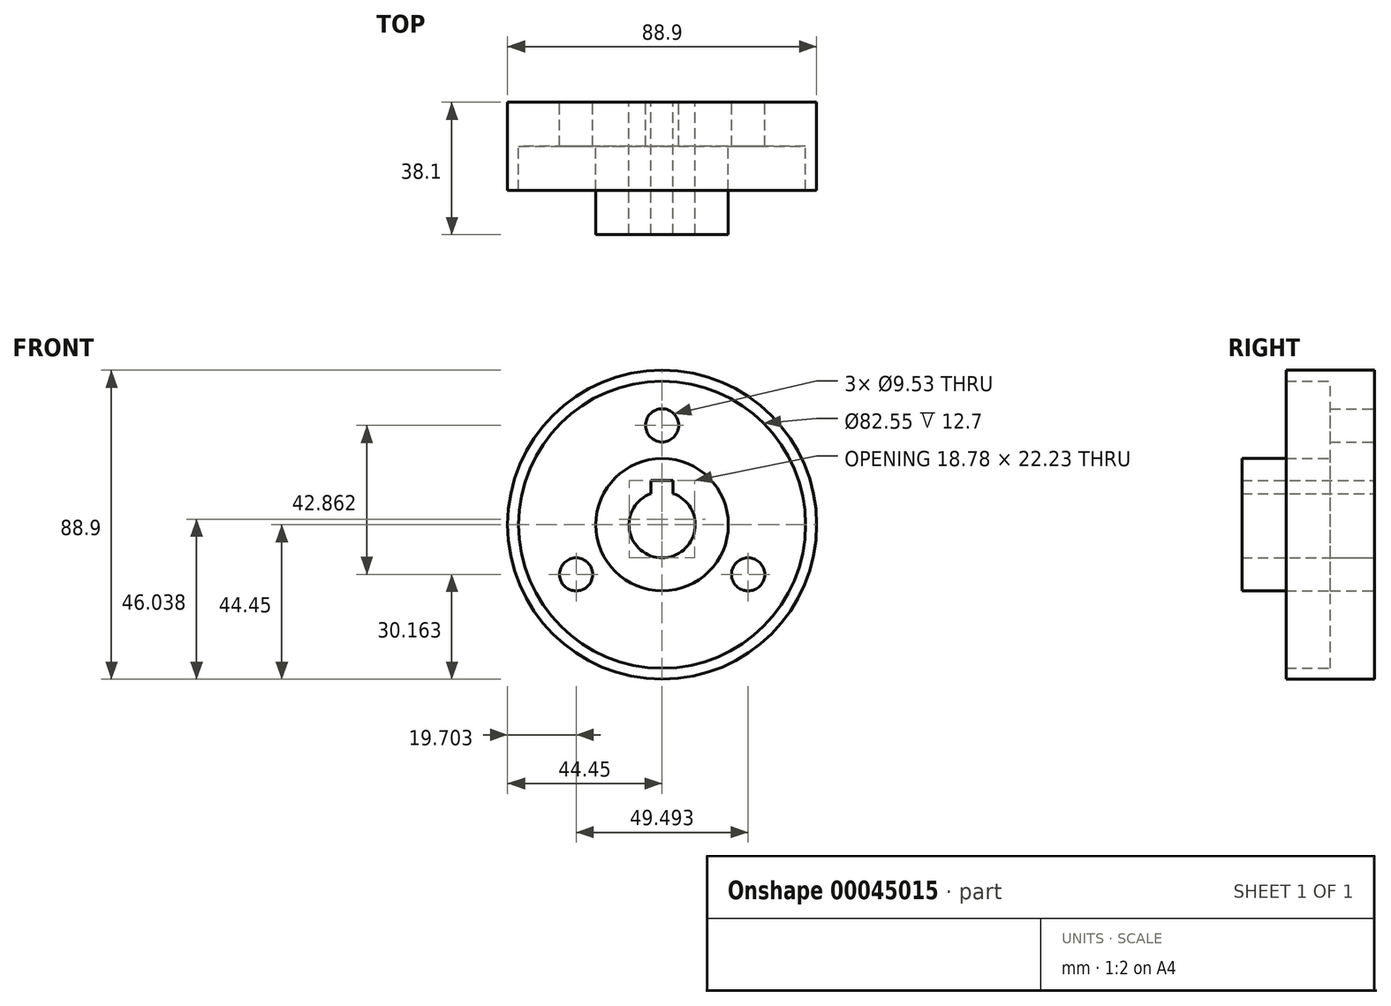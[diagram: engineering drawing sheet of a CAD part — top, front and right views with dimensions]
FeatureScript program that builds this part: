
annotation { "Feature Type Name" : "Feature", "Feature Type Description" : "" }
export const myFeature = defineFeature(function(context is Context, id is Id, definition is map)
    precondition{}
    {
        {
            var Q0;
            Q0=qCreatedBy(makeId("Front.planeOp"),FACE);
            var sketch = newSketch(context, id + "F0", { "sketchPlane" : qUnion([Q0])});
            skCircle(sketch, "E0", {"center": v(0, 0) * mm, "radius": 44.45 * mm});
            skSolve(sketch);
        }
        {
            var Q0;
            Q0 = qSketchRegion(id + "F0", true);
            extrude(context, id + "F1", {"entities" : qUnion([Q0]), "depth" : 12.7 * mm});
        }
        {
            var Q0;
            Q0=qCreatedBy(makeId("Front.planeOp"),FACE);
            var sketch = newSketch(context, id + "F2", { "sketchPlane" : qUnion([Q0])});
            skCircle(sketch, "E1", {"center": v(0, 0) * mm, "radius": 19.05 * mm});
            skSolve(sketch);
        }
        {
            var Q0;
            Q0 = qSketchRegion(id + "F2", true);
            extrude(context, id + "F3", {"entities" : qUnion([Q0]), "operationType" : NewBodyOperationType.ADD, "depth" : 38.1 * mm});
        }
        {
            var Q0;
            Q0=qCreatedBy(makeId("Front.planeOp"),FACE);
            var sketch = newSketch(context, id + "F4", { "sketchPlane" : qUnion([Q0])});
            skCircle(sketch, "E2", {"center": v(0, 0) * mm, "radius": 9.53 * mm});
            skSolve(sketch);
        }
        {
            var Q0;
            Q0 = qSketchRegion(id + "F4", true);
            extrude(context, id + "F5", {"entities" : qUnion([Q0]), "operationType" : NewBodyOperationType.REMOVE, "endBound" : BoundingType.THROUGH_ALL, "depth" : 25.4 * mm});
        }
        {
            var Q0;
            Q0=qCreatedBy(makeId("Front.planeOp"),FACE);
            var sketch = newSketch(context, id + "F6", { "sketchPlane" : qUnion([Q0])});
            skLineSegment(sketch, "E3.bottom", {"start": v(0, 0) * mm, "end": v(-3.18, 0) * mm});
            skLineSegment(sketch, "E3.top", {"start": v(0, 12.7) * mm, "end": v(-3.18, 12.7) * mm});
            skLineSegment(sketch, "E3.right", {"start": v(-3.18, 0) * mm, "end": v(-3.18, 12.7) * mm});
            skPoint(sketch, "E4", {"position": v(0, 0) * mm});
            skLineSegment(sketch, "E5.MirrorCS", {"start": v(0, 12.7) * mm, "end": v(3.18, 12.7) * mm});
            skLineSegment(sketch, "E6.MirrorCS", {"start": v(3.18, 0) * mm, "end": v(3.18, 12.7) * mm});
            skLineSegment(sketch, "E7.MirrorCS", {"start": v(0, 0) * mm, "end": v(3.18, 0) * mm});
            skSolve(sketch);
        }
        {
            var Q0;
            Q0 = qSketchRegion(id + "F6", true);
            extrude(context, id + "F7", {"entities" : qUnion([Q0]), "operationType" : NewBodyOperationType.REMOVE, "endBound" : BoundingType.THROUGH_ALL, "depth" : 25.4 * mm});
        }
        {
            var Q0;
            Q0=qCreatedBy(makeId("Front.planeOp"),FACE);
            var sketch = newSketch(context, id + "F8", { "sketchPlane" : qUnion([Q0])});
            skCircle(sketch, "E8", {"center": v(0, 0) * mm, "radius": 28.58 * mm, "construction": true});
            skCircle(sketch, "E9", {"center": v(0, 28.58) * mm, "radius": 4.76 * mm});
            skCircle(sketch, "E10.1.0", {"center": v(-24.75, -14.29) * mm, "radius": 4.76 * mm});
            skCircle(sketch, "E10.2.0", {"center": v(24.75, -14.29) * mm, "radius": 4.76 * mm});
            skSolve(sketch);
        }
        {
            var Q0;
            Q0 = qSketchRegion(id + "F8", true);
            extrude(context, id + "F9", {"entities" : qUnion([Q0]), "operationType" : NewBodyOperationType.REMOVE, "endBound" : BoundingType.THROUGH_ALL, "depth" : 25.4 * mm});
        }
        {
            var Q0;
            Q0=qCreatedBy(makeId("Front.planeOp"),FACE);
            var sketch = newSketch(context, id + "F10", { "sketchPlane" : qUnion([Q0])});
            skCircle(sketch, "E11", {"center": v(0, 0) * mm, "radius": 44.45 * mm});
            skCircle(sketch, "E12", {"center": v(0, 0) * mm, "radius": 41.28 * mm});
            skSolve(sketch);
        }
        {
            var Q0;
            Q0 = qSketchRegion(id + "F10", true);
            extrude(context, id + "F11", {"entities" : qUnion([Q0]), "operationType" : NewBodyOperationType.ADD, "depth" : 25.4 * mm});
        }
    });
